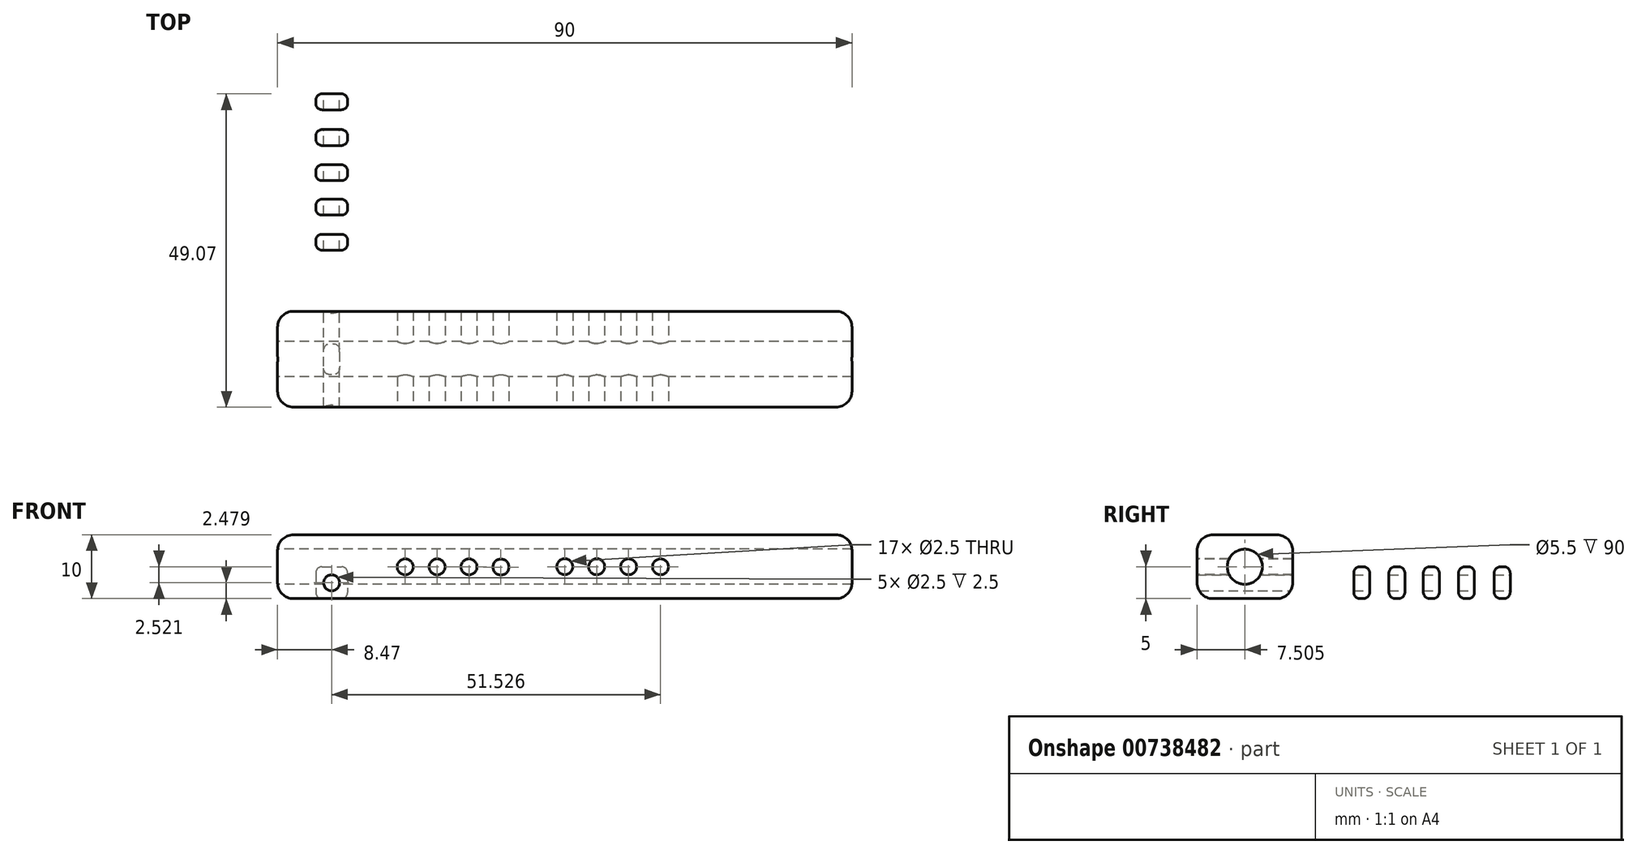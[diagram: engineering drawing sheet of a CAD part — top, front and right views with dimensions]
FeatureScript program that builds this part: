
annotation { "Feature Type Name" : "Feature", "Feature Type Description" : "" }
export const myFeature = defineFeature(function(context is Context, id is Id, definition is map)
    precondition{}
    {
        {
            var Q0;
            Q0=qCreatedBy(makeId("Top.planeOp"),FACE);
            var sketch = newSketch(context, id + "F0", { "sketchPlane" : qUnion([Q0])});
            skLineSegment(sketch, "E0.bottom", {"start": v(-45.71, 9.17) * mm, "end": v(44.29, 9.17) * mm});
            skLineSegment(sketch, "E0.top", {"start": v(-45.71, -5.83) * mm, "end": v(44.29, -5.83) * mm});
            skLineSegment(sketch, "E0.left", {"start": v(-45.71, 9.17) * mm, "end": v(-45.71, -5.83) * mm});
            skLineSegment(sketch, "E0.right", {"start": v(44.29, 9.17) * mm, "end": v(44.29, -5.83) * mm});
            skSolve(sketch);
        }
        {
            var Q0;
            Q0=makeQuery(id+"F0.imprint","IMPRINT",FACE,{"disambiguationData":[TD([[makeQuery(id+"F0.imprint","IMPRINT",EDGE,{"derivedFrom":sQuery(id+"F0.wireOp",EDGE,"E0.bottom")}),-1.0]])]});
            extrude(context, id + "F1", {"entities" : qUnion([Q0]), "depth" : 10 * mm, "offsetDistance" : 25 * mm});
        }
        {
            var Q0;
            Q0=makeQuery(id+"F1.opExtrude","SWEPT_FACE",FACE,{"disambiguationData":[OSD([sQuery(id+"F0.wireOp",EDGE,"E0.left")])]});
            var sketch = newSketch(context, id + "F2", { "sketchPlane" : qUnion([Q0])});
            skCircle(sketch, "E1", {"center": v(-1.67, 5) * mm, "radius": 2.75 * mm});
            skPoint(sketch, "E1.centerSnap0", {"position": v(-9.17, 5) * mm});
            skPoint(sketch, "E1.centerSnap1", {"position": v(-1.67, 10) * mm});
            skSolve(sketch);
        }
        {
            var Q0;
            Q0=makeQuery(id+"F2.imprint","IMPRINT",FACE,{"disambiguationData":[TD([[makeQuery(id+"F2.imprint","IMPRINT",EDGE,{"derivedFrom":sQuery(id+"F2.wireOp",EDGE,"E1")}),1.0]])]});
            extrude(context, id + "F3", {"entities" : qUnion([Q0]), "operationType" : NewBodyOperationType.REMOVE, "endBound" : BoundingType.THROUGH_ALL, "oppositeDirection" : true, "depth" : 25 * mm, "offsetDistance" : 25 * mm});
        }
        {
            var Q0;
            Q0=makeQuery(id+"F1.opExtrude","SWEPT_FACE",FACE,{"disambiguationData":[OSD([sQuery(id+"F0.wireOp",EDGE,"E0.top")])]});
            var sketch = newSketch(context, id + "F4", { "sketchPlane" : qUnion([Q0])});
            skCircle(sketch, "E2", {"center": v(-25.71, 4.97) * mm, "radius": 1.25 * mm});
            skCircle(sketch, "E3", {"center": v(-20.71, 4.97) * mm, "radius": 1.25 * mm});
            skCircle(sketch, "E4", {"center": v(-15.71, 4.97) * mm, "radius": 1.25 * mm});
            skCircle(sketch, "E5", {"center": v(-10.71, 4.94) * mm, "radius": 1.25 * mm});
            skCircle(sketch, "E6", {"center": v(-0.71, 5) * mm, "radius": 1.25 * mm});
            skCircle(sketch, "E7", {"center": v(4.29, 5) * mm, "radius": 1.25 * mm});
            skCircle(sketch, "E8", {"center": v(9.29, 4.99) * mm, "radius": 1.25 * mm});
            skCircle(sketch, "E9", {"center": v(14.29, 4.99) * mm, "radius": 1.25 * mm});
            skPoint(sketch, "E10", {"position": v(44.29, 5) * mm});
            skPoint(sketch, "E11", {"position": v(-0.71, 10) * mm});
            skSolve(sketch);
        }
        {
            var Q0;
            Q0=makeQuery(id+"F4.imprint","IMPRINT",FACE,{"disambiguationData":[TD([[makeQuery(id+"F4.imprint","IMPRINT",EDGE,{"derivedFrom":sQuery(id+"F4.wireOp",EDGE,"E2")}),1.0]])]});
            var Q1;
            Q1=makeQuery(id+"F4.imprint","IMPRINT",FACE,{"disambiguationData":[TD([[makeQuery(id+"F4.imprint","IMPRINT",EDGE,{"derivedFrom":sQuery(id+"F4.wireOp",EDGE,"E3")}),1.0]])]});
            var Q2;
            Q2=makeQuery(id+"F4.imprint","IMPRINT",FACE,{"disambiguationData":[TD([[makeQuery(id+"F4.imprint","IMPRINT",EDGE,{"derivedFrom":sQuery(id+"F4.wireOp",EDGE,"E4")}),1.0]])]});
            var Q3;
            Q3=makeQuery(id+"F4.imprint","IMPRINT",FACE,{"disambiguationData":[TD([[makeQuery(id+"F4.imprint","IMPRINT",EDGE,{"derivedFrom":sQuery(id+"F4.wireOp",EDGE,"E5")}),1.0]])]});
            var Q4;
            Q4=makeQuery(id+"F4.imprint","IMPRINT",FACE,{"disambiguationData":[TD([[makeQuery(id+"F4.imprint","IMPRINT",EDGE,{"derivedFrom":sQuery(id+"F4.wireOp",EDGE,"E6")}),1.0]])]});
            var Q5;
            Q5=makeQuery(id+"F4.imprint","IMPRINT",FACE,{"disambiguationData":[TD([[makeQuery(id+"F4.imprint","IMPRINT",EDGE,{"derivedFrom":sQuery(id+"F4.wireOp",EDGE,"E6")}),1.0]])]});
            var Q6;
            Q6=makeQuery(id+"F4.imprint","IMPRINT",FACE,{"disambiguationData":[TD([[makeQuery(id+"F4.imprint","IMPRINT",EDGE,{"derivedFrom":sQuery(id+"F4.wireOp",EDGE,"E7")}),1.0]])]});
            var Q7;
            Q7=makeQuery(id+"F4.imprint","IMPRINT",FACE,{"disambiguationData":[TD([[makeQuery(id+"F4.imprint","IMPRINT",EDGE,{"derivedFrom":sQuery(id+"F4.wireOp",EDGE,"E8")}),1.0]])]});
            var Q8;
            Q8=makeQuery(id+"F4.imprint","IMPRINT",FACE,{"disambiguationData":[TD([[makeQuery(id+"F4.imprint","IMPRINT",EDGE,{"derivedFrom":sQuery(id+"F4.wireOp",EDGE,"E9")}),1.0]])]});
            extrude(context, id + "F5", {"entities" : qUnion([Q0, Q1, Q2, Q3, Q4, Q5, Q6, Q7, Q8]), "operationType" : NewBodyOperationType.REMOVE, "endBound" : BoundingType.THROUGH_ALL, "oppositeDirection" : true, "depth" : 25 * mm, "offsetDistance" : 25 * mm});
        }
        {
            var Q0;
            Q0=makeQuery(id+"F1.opExtrude","CAP_FACE",FACE,{"disambiguationData":[OSD([sQuery(id+"F0.wireOp",EDGE,"E0.bottom"),sQuery(id+"F0.wireOp",EDGE,"E0.top"),sQuery(id+"F0.wireOp",EDGE,"E0.left"),sQuery(id+"F0.wireOp",EDGE,"E0.right")])],"isStart":false});
            var Q1;
            Q1=makeQuery(id+"F1.opExtrude","CAP_FACE",FACE,{"disambiguationData":[OSD([sQuery(id+"F0.wireOp",EDGE,"E0.bottom"),sQuery(id+"F0.wireOp",EDGE,"E0.top"),sQuery(id+"F0.wireOp",EDGE,"E0.left"),sQuery(id+"F0.wireOp",EDGE,"E0.right")])],"isStart":true});
            var Q2;
            Q2=makeQuery(id+"F1.opExtrude","SWEPT_EDGE",EDGE,{"disambiguationData":[OSD([sQuery(id+"F0.wireOp",EDGE,"E0.bottom"),sQuery(id+"F0.wireOp",EDGE,"E0.right")])]});
            var Q3;
            Q3=makeQuery(id+"F1.opExtrude","SWEPT_EDGE",EDGE,{"disambiguationData":[OSD([sQuery(id+"F0.wireOp",EDGE,"E0.top"),sQuery(id+"F0.wireOp",EDGE,"E0.right")])]});
            var Q4;
            Q4=makeQuery(id+"F1.opExtrude","SWEPT_EDGE",EDGE,{"disambiguationData":[OSD([sQuery(id+"F0.wireOp",EDGE,"E0.top"),sQuery(id+"F0.wireOp",EDGE,"E0.left")])]});
            var Q5;
            Q5=makeQuery(id+"F1.opExtrude","SWEPT_EDGE",EDGE,{"disambiguationData":[OSD([sQuery(id+"F0.wireOp",EDGE,"E0.bottom"),sQuery(id+"F0.wireOp",EDGE,"E0.left")])]});
            fillet(context, id + "F6", {"entities" : qUnion([Q0, Q1, Q2, Q3, Q4, Q5]), "radius" : 2.5 * mm, "tangentPropagation" : true, "allowEdgeOverflow" : false});
        }
        {
            var Q0;
            Q0=qCreatedBy(makeId("Top.planeOp"),FACE);
            var sketch = newSketch(context, id + "F7", { "sketchPlane" : qUnion([Q0])});
            skLineSegment(sketch, "E12.bottom", {"start": v(-39.72, 21.24) * mm, "end": v(-34.72, 21.24) * mm});
            skLineSegment(sketch, "E12.top", {"start": v(-39.72, 18.74) * mm, "end": v(-34.72, 18.74) * mm});
            skLineSegment(sketch, "E12.left", {"start": v(-39.72, 21.24) * mm, "end": v(-39.72, 18.74) * mm});
            skLineSegment(sketch, "E12.right", {"start": v(-34.72, 21.24) * mm, "end": v(-34.72, 18.74) * mm});
            skSolve(sketch);
        }
        {
            var Q0;
            Q0=makeQuery(id+"F7.imprint","IMPRINT",FACE,{"disambiguationData":[TD([[makeQuery(id+"F7.imprint","IMPRINT",EDGE,{"derivedFrom":sQuery(id+"F7.wireOp",EDGE,"E12.bottom")}),-1.0]])]});
            extrude(context, id + "F8", {"entities" : qUnion([Q0]), "depth" : 5 * mm, "offsetDistance" : 25 * mm});
        }
        {
            var Q0;
            Q0=makeQuery(id+"F8.opExtrude","SWEPT_FACE",FACE,{"disambiguationData":[OSD([sQuery(id+"F7.wireOp",EDGE,"E12.bottom")])]});
            var sketch = newSketch(context, id + "F9", { "sketchPlane" : qUnion([Q0])});
            skSolve(sketch);
        }
        {
            var Q0;
            {var subQ0=sQuery(id+"F7.wireOp",EDGE,"E12.bottom");Q0=makeQuery(id+"F9.imprint","IMPRINT",FACE,{"disambiguationData":[TD([[makeQuery(id+"F9.imprint","IMPRINT",EDGE,{"derivedFrom":makeQuery(id+"F8.opExtrude","CAP_EDGE",EDGE,{"disambiguationData":[OSD([subQ0])],"isStart":true})}),-1.0]])]});}
            var sketch = newSketch(context, id + "F10", { "sketchPlane" : qUnion([Q0])});
            skCircle(sketch, "E13", {"center": v(37.24, 2.48) * mm, "radius": 1.25 * mm});
            skSolve(sketch);
        }
        {
            var Q0;
            Q0=makeQuery(id+"F10.imprint","IMPRINT",FACE,{"disambiguationData":[TD([[makeQuery(id+"F10.imprint","IMPRINT",EDGE,{"derivedFrom":sQuery(id+"F10.wireOp",EDGE,"E13")}),1.0]])]});
            extrude(context, id + "F11", {"entities" : qUnion([Q0]), "operationType" : NewBodyOperationType.REMOVE, "endBound" : BoundingType.THROUGH_ALL, "oppositeDirection" : true, "depth" : 25 * mm, "offsetDistance" : 25 * mm});
        }
        {
            var Q0;
            Q0=makeQuery(id+"F8.opExtrude","CAP_FACE",FACE,{"disambiguationData":[OSD([sQuery(id+"F7.wireOp",EDGE,"E12.bottom"),sQuery(id+"F7.wireOp",EDGE,"E12.top"),sQuery(id+"F7.wireOp",EDGE,"E12.left"),sQuery(id+"F7.wireOp",EDGE,"E12.right")])],"isStart":false});
            var Q1;
            Q1=makeQuery(id+"F8.opExtrude","SWEPT_FACE",FACE,{"disambiguationData":[OSD([sQuery(id+"F7.wireOp",EDGE,"E12.left")])]});
            var Q2;
            Q2=makeQuery(id+"F8.opExtrude","CAP_FACE",FACE,{"disambiguationData":[OSD([sQuery(id+"F7.wireOp",EDGE,"E12.bottom"),sQuery(id+"F7.wireOp",EDGE,"E12.top"),sQuery(id+"F7.wireOp",EDGE,"E12.left"),sQuery(id+"F7.wireOp",EDGE,"E12.right")])],"isStart":true});
            var Q3;
            Q3=makeQuery(id+"F8.opExtrude","SWEPT_FACE",FACE,{"disambiguationData":[OSD([sQuery(id+"F7.wireOp",EDGE,"E12.right")])]});
            fillet(context, id + "F12", {"entities" : qUnion([Q0, Q1, Q2, Q3]), "radius" : 1 * mm, "tangentPropagation" : true, "allowEdgeOverflow" : false});
        }
        {
            var Q0;
            Q0=makeQuery(id+"F8.opExtrude","SWEPT_BODY",BODY,{"disambiguationData":[OSD([sQuery(id+"F7.wireOp",EDGE,"E12.bottom"),sQuery(id+"F7.wireOp",EDGE,"E12.top"),sQuery(id+"F7.wireOp",EDGE,"E12.left"),sQuery(id+"F7.wireOp",EDGE,"E12.right")])]});
            transform(context, id + "F13", {"entities" : qUnion([Q0]), "transformType" : TransformType.TRANSLATION_3D, "dx" : 0 * mm, "dy" : 0 * mm, "dz" : 0 * mm, "makeCopy" : true});
        }
        {
            var Q0;
            Q0=makeQuery(id+"F8.opExtrude","SWEPT_BODY",BODY,{"disambiguationData":[OSD([sQuery(id+"F7.wireOp",EDGE,"E12.bottom"),sQuery(id+"F7.wireOp",EDGE,"E12.top"),sQuery(id+"F7.wireOp",EDGE,"E12.left"),sQuery(id+"F7.wireOp",EDGE,"E12.right")])]});
            deleteBodies(context, id + "F14", {"entities" : qUnion([Q0])});
        }
        {
            var Q0;
            Q0=makeQuery(id+"F13.opPattern","COPY",BODY,{"derivedFrom":makeQuery(id+"F8.opExtrude","SWEPT_BODY",BODY,{"disambiguationData":[OSD([sQuery(id+"F7.wireOp",EDGE,"E12.bottom"),sQuery(id+"F7.wireOp",EDGE,"E12.top"),sQuery(id+"F7.wireOp",EDGE,"E12.left"),sQuery(id+"F7.wireOp",EDGE,"E12.right")])]}),"instanceName":"1"});
            transform(context, id + "F15", {"entities" : qUnion([Q0]), "transformType" : TransformType.TRANSLATION_3D, "dx" : 0 * mm, "dy" : 5.5 * mm, "dz" : 0 * mm, "makeCopy" : true});
        }
        {
            var Q0;
            Q0=makeQuery(id+"F15.opPattern","COPY",BODY,{"derivedFrom":makeQuery(id+"F13.opPattern","COPY",BODY,{"derivedFrom":makeQuery(id+"F8.opExtrude","SWEPT_BODY",BODY,{"disambiguationData":[OSD([sQuery(id+"F7.wireOp",EDGE,"E12.bottom"),sQuery(id+"F7.wireOp",EDGE,"E12.top"),sQuery(id+"F7.wireOp",EDGE,"E12.left"),sQuery(id+"F7.wireOp",EDGE,"E12.right")])]}),"instanceName":"1"}),"instanceName":"1"});
            transform(context, id + "F16", {"entities" : qUnion([Q0]), "transformType" : TransformType.TRANSLATION_3D, "dx" : 0 * mm, "dy" : 5.4 * mm, "dz" : 0 * mm, "makeCopy" : true});
        }
        {
            var Q0;
            Q0=makeQuery(id+"F16.opPattern","COPY",BODY,{"derivedFrom":makeQuery(id+"F15.opPattern","COPY",BODY,{"derivedFrom":makeQuery(id+"F13.opPattern","COPY",BODY,{"derivedFrom":makeQuery(id+"F8.opExtrude","SWEPT_BODY",BODY,{"disambiguationData":[OSD([sQuery(id+"F7.wireOp",EDGE,"E12.bottom"),sQuery(id+"F7.wireOp",EDGE,"E12.top"),sQuery(id+"F7.wireOp",EDGE,"E12.left"),sQuery(id+"F7.wireOp",EDGE,"E12.right")])]}),"instanceName":"1"}),"instanceName":"1"}),"instanceName":"1"});
            transform(context, id + "F17", {"entities" : qUnion([Q0]), "transformType" : TransformType.TRANSLATION_3D, "dx" : 0 * mm, "dy" : 5.5 * mm, "dz" : 0 * mm, "makeCopy" : true});
        }
        {
            var Q0;
            Q0=makeQuery(id+"F17.opPattern","COPY",BODY,{"derivedFrom":makeQuery(id+"F16.opPattern","COPY",BODY,{"derivedFrom":makeQuery(id+"F15.opPattern","COPY",BODY,{"derivedFrom":makeQuery(id+"F13.opPattern","COPY",BODY,{"derivedFrom":makeQuery(id+"F8.opExtrude","SWEPT_BODY",BODY,{"disambiguationData":[OSD([sQuery(id+"F7.wireOp",EDGE,"E12.bottom"),sQuery(id+"F7.wireOp",EDGE,"E12.top"),sQuery(id+"F7.wireOp",EDGE,"E12.left"),sQuery(id+"F7.wireOp",EDGE,"E12.right")])]}),"instanceName":"1"}),"instanceName":"1"}),"instanceName":"1"}),"instanceName":"1"});
            transform(context, id + "F18", {"entities" : qUnion([Q0]), "transformType" : TransformType.TRANSLATION_3D, "dx" : 0 * mm, "dy" : 5.6 * mm, "dz" : 0 * mm, "makeCopy" : true});
        }
    });
